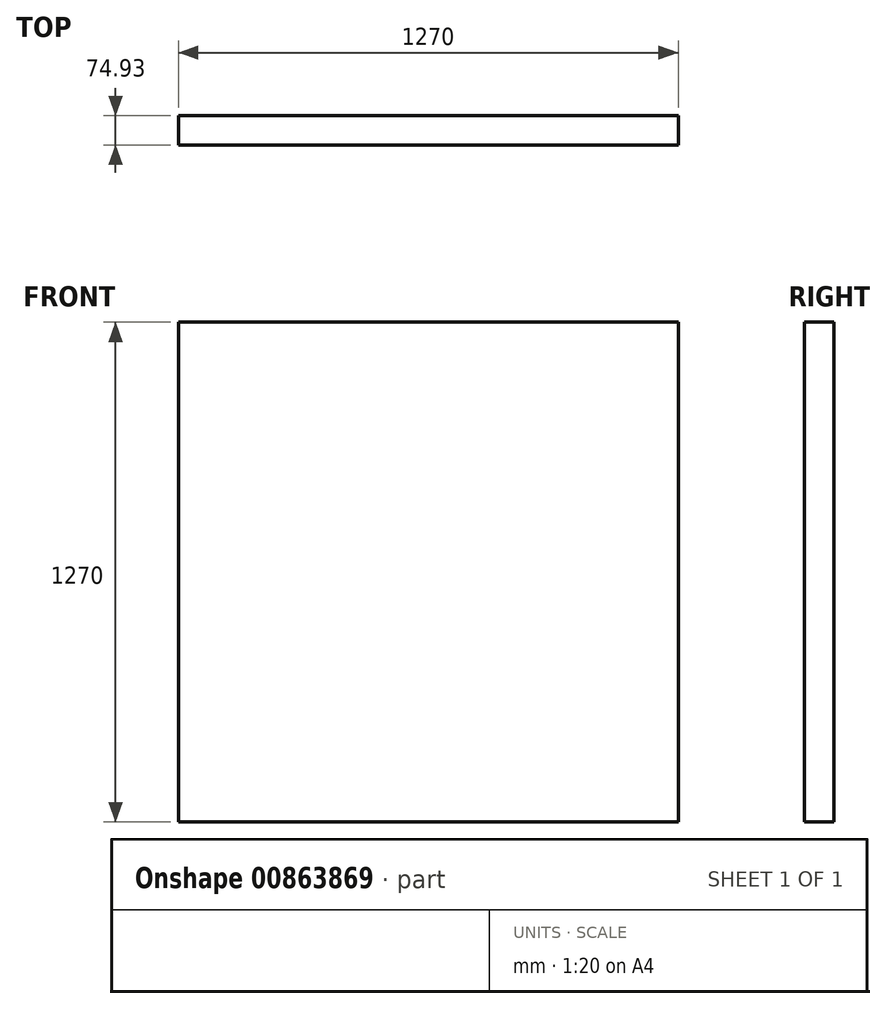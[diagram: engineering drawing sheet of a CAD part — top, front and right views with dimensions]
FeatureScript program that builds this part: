
annotation { "Feature Type Name" : "Feature", "Feature Type Description" : "" }
export const myFeature = defineFeature(function(context is Context, id is Id, definition is map)
    precondition{}
    {
        {
            var Q0;
            Q0=qCreatedBy(makeId("Front.planeOp"),FACE);
            var sketch = newSketch(context, id + "F0", { "sketchPlane" : qUnion([Q0])});
            skLineSegment(sketch, "E0", {"start": v(0, 0) * mm, "end": v(0, 1270) * mm});
            skLineSegment(sketch, "E1", {"start": v(0, 1270) * mm, "end": v(1270, 1270) * mm});
            skLineSegment(sketch, "E2", {"start": v(1270, 1270) * mm, "end": v(1270, 0) * mm});
            skLineSegment(sketch, "E3", {"start": v(1270, 0) * mm, "end": v(0, 0) * mm});
            skSolve(sketch);
        }
        {
            var Q0;
            Q0 = qSketchRegion(id + "F0", true);
            extrude(context, id + "F1", {"entities" : qUnion([Q0]), "depth" : 74.93 * mm, "offsetDistance" : 25.4 * mm});
        }
    });
